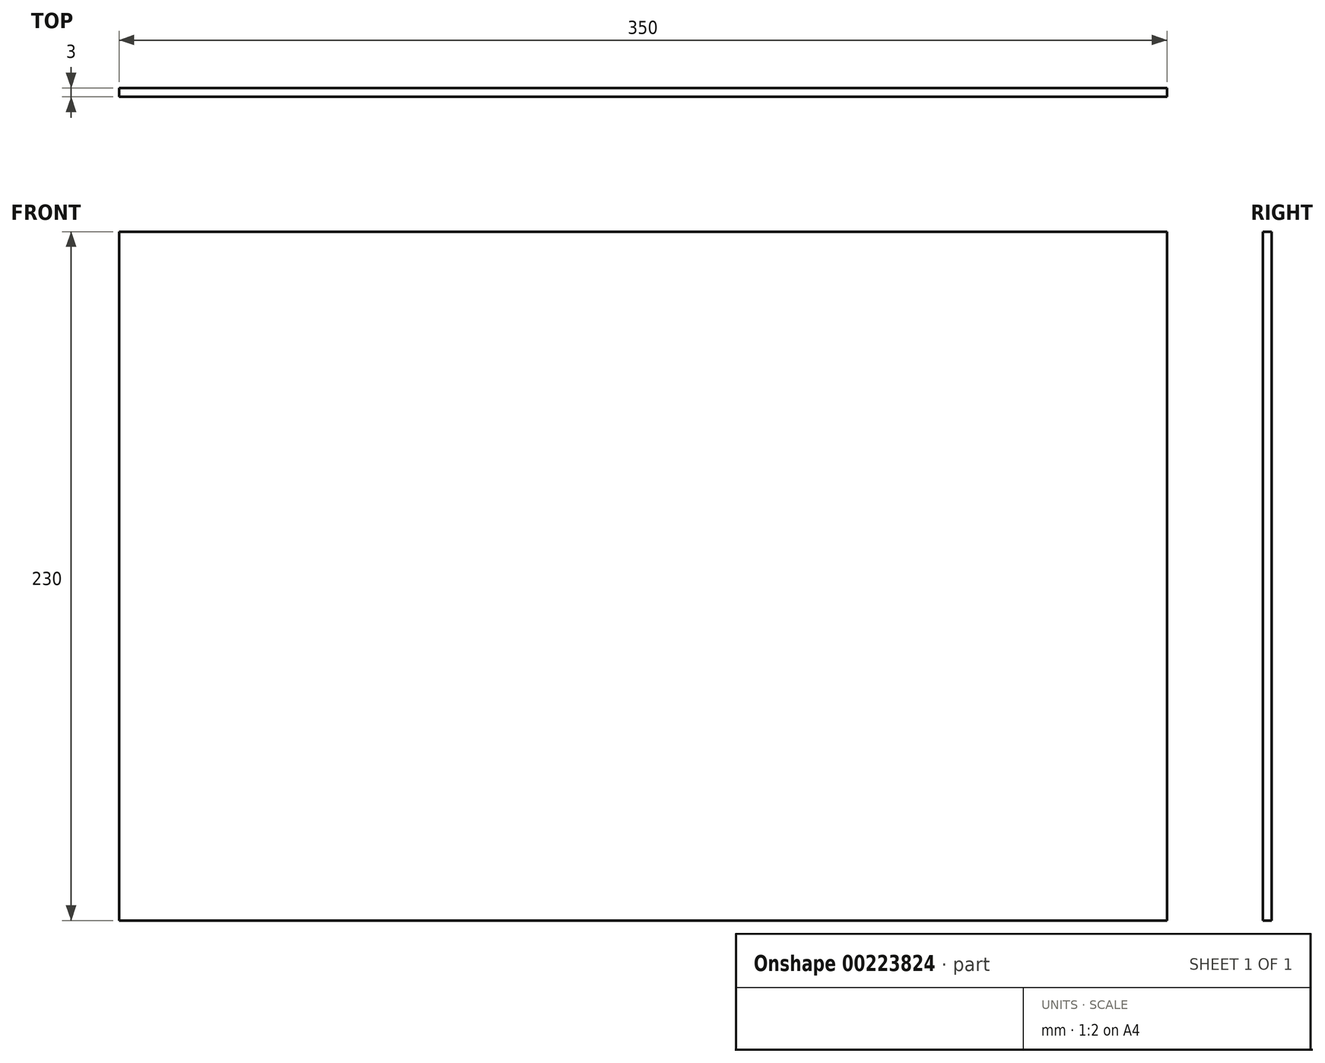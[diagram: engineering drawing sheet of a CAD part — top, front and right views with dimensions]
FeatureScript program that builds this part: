
annotation { "Feature Type Name" : "Feature", "Feature Type Description" : "" }
export const myFeature = defineFeature(function(context is Context, id is Id, definition is map)
    precondition{}
    {
        {
            var Q0;
            Q0=qCreatedBy(makeId("Front.planeOp"),FACE);
            var sketch = newSketch(context, id + "F0", { "sketchPlane" : qUnion([Q0])});
            skLineSegment(sketch, "E0.bottom", {"start": v(-175, 50) * mm, "end": v(175, 50) * mm});
            skLineSegment(sketch, "E0.top", {"start": v(-175, -180) * mm, "end": v(175, -180) * mm});
            skLineSegment(sketch, "E0.left", {"start": v(-175, 50) * mm, "end": v(-175, -180) * mm});
            skLineSegment(sketch, "E0.right", {"start": v(175, 50) * mm, "end": v(175, -180) * mm});
            skSolve(sketch);
        }
        {
            var Q0;
            Q0 = qSketchRegion(id + "F0", true);
            extrude(context, id + "F1", {"entities" : qUnion([Q0]), "depth" : 3 * mm});
        }
    });
